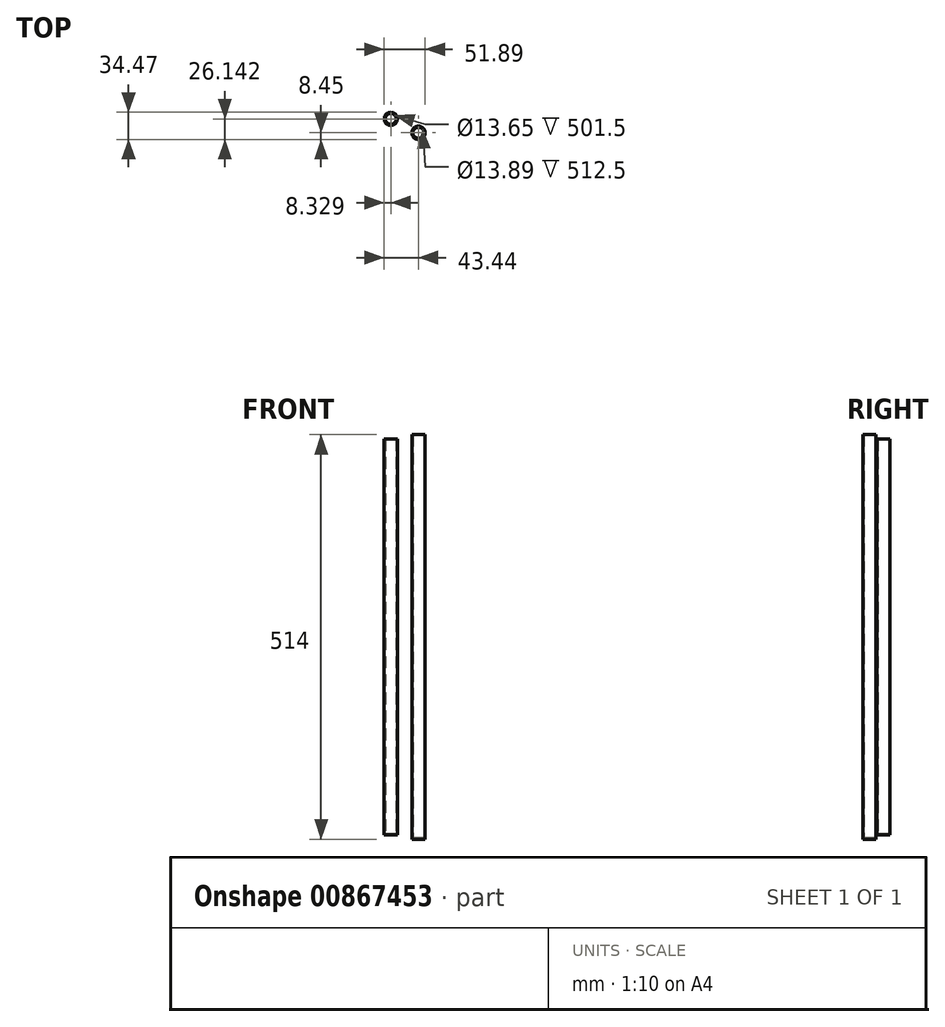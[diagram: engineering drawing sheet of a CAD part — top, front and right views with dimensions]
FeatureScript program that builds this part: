
annotation { "Feature Type Name" : "Feature", "Feature Type Description" : "" }
export const myFeature = defineFeature(function(context is Context, id is Id, definition is map)
    precondition{}
    {
        {
            var Q0;
            Q0=qCreatedBy(makeId("Top.planeOp"),FACE);
            var sketch = newSketch(context, id + "F0", { "sketchPlane" : qUnion([Q0])});
            skCircle(sketch, "E0", {"center": v(0, 0) * mm, "radius": 8.45 * mm});
            skSolve(sketch);
        }
        {
            var Q0;
            Q0=makeQuery(id+"F0.imprint","IMPRINT",FACE,{"disambiguationData":[TD([[makeQuery(id+"F0.imprint","IMPRINT",EDGE,{"derivedFrom":sQuery(id+"F0.wireOp",EDGE,"E0")}),1.0]])]});
            extrude(context, id + "F1", {"entities" : qUnion([Q0]), "endBound" : BoundingType.SYMMETRIC, "depth" : 514 * mm, "offsetDistance" : 25 * mm});
        }
        {
            var Q0;
            Q0=qCreatedBy(makeId("Top.planeOp"),FACE);
            var sketch = newSketch(context, id + "F2", { "sketchPlane" : qUnion([Q0])});
            skCircle(sketch, "E1", {"center": v(-35.11, 17.7) * mm, "radius": 8.33 * mm});
            skSolve(sketch);
        }
        {
            var Q0;
            Q0=makeQuery(id+"F2.imprint","IMPRINT",FACE,{"disambiguationData":[TD([[makeQuery(id+"F2.imprint","IMPRINT",EDGE,{"derivedFrom":sQuery(id+"F2.wireOp",EDGE,"E1")}),1.0]])]});
            extrude(context, id + "F3", {"entities" : qUnion([Q0]), "endBound" : BoundingType.SYMMETRIC, "depth" : 503 * mm, "offsetDistance" : 25 * mm});
        }
        {
            var Q0;
            Q0=makeQuery(id+"F3.opExtrude","CAP_FACE",FACE,{"disambiguationData":[OSD([sQuery(id+"F2.wireOp",EDGE,"E1")])],"isStart":false});
            var Q1;
            Q1=makeQuery(id+"F1.opExtrude","CAP_FACE",FACE,{"disambiguationData":[OSD([sQuery(id+"F0.wireOp",EDGE,"E0")])],"isStart":false});
            shell(context, id + "F4", {"entities" : qUnion([Q0, Q1]), "thickness" : 1.5 * mm});
        }
    });
